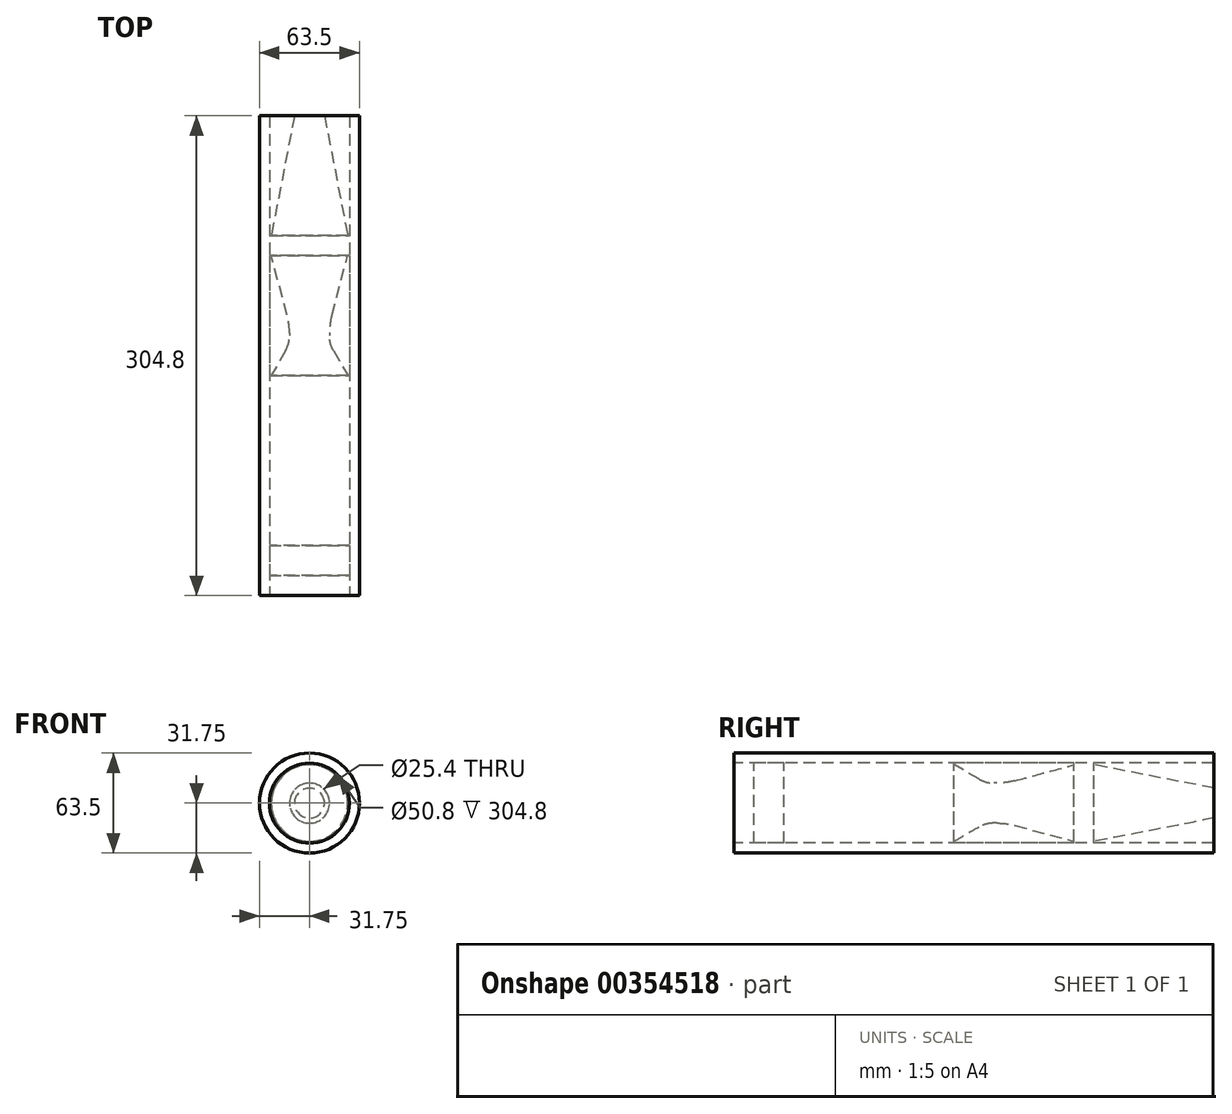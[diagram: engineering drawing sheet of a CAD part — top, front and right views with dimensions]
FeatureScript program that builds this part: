
annotation { "Feature Type Name" : "Feature", "Feature Type Description" : "" }
export const myFeature = defineFeature(function(context is Context, id is Id, definition is map)
    precondition{}
    {
        {
            var Q0;
            Q0=qCreatedBy(makeId("Front.planeOp"),FACE);
            var sketch = newSketch(context, id + "F0", { "sketchPlane" : qUnion([Q0])});
            skCircle(sketch, "E0", {"center": v(0, 0) * mm, "radius": 31.75 * mm});
            skCircle(sketch, "E1", {"center": v(0, 0) * mm, "radius": 25.4 * mm});
            skCircle(sketch, "E2", {"center": v(0, 0) * mm, "radius": 12.7 * mm});
            skCircle(sketch, "E3", {"center": v(0, 0) * mm, "radius": 9.53 * mm});
            skSolve(sketch);
        }
        {
            var Q0;
            Q0 = qSketchRegion(id + "F0", true);
            extrude(context, id + "F1", {"entities" : qUnion([Q0]), "oppositeDirection" : true, "offsetDistance" : 25.4 * mm, "depth" : 304.8 * mm});
        }
        {
            var Q0;
            Q0=makeQuery(id+"F0.imprint","IMPRINT",FACE,{"disambiguationData":[TD([[makeQuery(id+"F0.imprint","IMPRINT",EDGE,{"derivedFrom":sQuery(id+"F0.wireOp",EDGE,"E1")}),1.0]])]});
            extrude(context, id + "F2", {"entities" : qUnion([Q0]), "oppositeDirection" : true, "depth" : 76.2 * mm, "offsetDistance" : 25.4 * mm});
        }
        {
            var Q0;
            Q0=makeQuery(id+"F2.opExtrude","SWEPT_BODY",BODY,{"disambiguationData":[OSD([sQuery(id+"F0.wireOp",EDGE,"E1"),sQuery(id+"F0.wireOp",EDGE,"E2")])]});
            transform(context, id + "F3", {"entities" : qUnion([Q0]), "transformType" : TransformType.TRANSLATION_3D, "dx" : 127 * mm, "dy" : 0 * mm, "dz" : 0 * mm, "makeCopy" : false});
        }
        {
            var Q0;
            Q0=makeQuery(id+"F0.imprint","IMPRINT",FACE,{"disambiguationData":[TD([[makeQuery(id+"F0.imprint","IMPRINT",EDGE,{"derivedFrom":sQuery(id+"F0.wireOp",EDGE,"E1")}),1.0]])]});
            var Q1;
            Q1=makeQuery(id+"F0.imprint","IMPRINT",FACE,{"disambiguationData":[TD([[makeQuery(id+"F0.imprint","IMPRINT",EDGE,{"derivedFrom":sQuery(id+"F0.wireOp",EDGE,"E2")}),1.0]])]});
            extrude(context, id + "F4", {"entities" : qUnion([Q0, Q1]), "oppositeDirection" : true, "depth" : 76.2 * mm, "offsetDistance" : 25.4 * mm});
        }
        {
            var Q0;
            Q0=makeQuery(id+"F4.opExtrude","SWEPT_BODY",BODY,{"disambiguationData":[OSD([sQuery(id+"F0.wireOp",EDGE,"E1"),sQuery(id+"F0.wireOp",EDGE,"E3")])]});
            transform(context, id + "F5", {"entities" : qUnion([Q0]), "transformType" : TransformType.TRANSLATION_3D, "dx" : -127 * mm, "dy" : 0 * mm, "dz" : 0 * mm, "makeCopy" : false});
        }
        {
            var Q0;
            Q0=makeQuery(id+"F2.opExtrude","CAP_EDGE",EDGE,{"disambiguationData":[OSD([sQuery(id+"F0.wireOp",EDGE,"E2")])],"isStart":true});
            chamfer(context, id + "F6", {"entities" : qUnion([Q0]), "chamferType" : ChamferType.OFFSET_ANGLE, "width" : 20.32 * mm, "oppositeDirection" : false, "angle" : 30 * degree, "tangentPropagation" : true});
        }
        {
            var Q0;
            Q0=makeQuery(id+"F2.opExtrude","CAP_EDGE",EDGE,{"disambiguationData":[OSD([sQuery(id+"F0.wireOp",EDGE,"E2")])],"isStart":false});
            chamfer(context, id + "F7", {"entities" : qUnion([Q0]), "chamferType" : ChamferType.OFFSET_ANGLE, "width" : 43.18 * mm, "oppositeDirection" : true, "angle" : 15 * degree, "tangentPropagation" : true});
        }
        {
            var Q0;
            {var subQ0=sQuery(id+"F0.wireOp",EDGE,"E2");Q0=makeQuery(id+"F6.opChamfer","BLEND_EDGE",EDGE,{"blendedFrom":[makeQuery(id+"F2.opExtrude","CAP_EDGE",EDGE,{"disambiguationData":[OSD([subQ0])],"isStart":true}),makeQuery(id+"F2.opExtrude","SWEPT_FACE",FACE,{"disambiguationData":[OSD([subQ0])]})],"blendedInto":[makeQuery(id+"F2.opExtrude","SWEPT_FACE",FACE,{"disambiguationData":[OSD([subQ0])]})]});}
            fillet(context, id + "F8", {"entities" : qUnion([Q0]), "tangentPropagation" : true, "radius" : 19.05 * mm, "defaultsChanged" : true, "vertexSettings" : [], "allowEdgeOverflow" : false});
        }
        {
            var Q0;
            {var subQ0=sQuery(id+"F0.wireOp",EDGE,"E2");Q0=makeQuery(id+"F7.opChamfer","BLEND_EDGE",EDGE,{"blendedFrom":[makeQuery(id+"F2.opExtrude","CAP_EDGE",EDGE,{"disambiguationData":[OSD([subQ0])],"isStart":false}),makeQuery(id+"F2.opExtrude","SWEPT_FACE",FACE,{"disambiguationData":[OSD([subQ0])]})],"blendedInto":[makeQuery(id+"F2.opExtrude","SWEPT_FACE",FACE,{"disambiguationData":[OSD([subQ0])]})]});}
            fillet(context, id + "F9", {"entities" : qUnion([Q0]), "tangentPropagation" : true, "radius" : 44.45 * mm, "defaultsChanged" : true, "vertexSettings" : [], "allowEdgeOverflow" : false});
        }
        {
            var Q0;
            Q0=makeQuery(id+"F4.opExtrude","CAP_EDGE",EDGE,{"disambiguationData":[OSD([sQuery(id+"F0.wireOp",EDGE,"E3")])],"isStart":true});
            chamfer(context, id + "F10", {"entities" : qUnion([Q0]), "chamferType" : ChamferType.OFFSET_ANGLE, "width" : 76.2 * mm, "oppositeDirection" : false, "angle" : 11 * degree, "tangentPropagation" : true});
        }
        {
            var Q0;
            Q0=makeQuery(id+"F4.opExtrude","SWEPT_BODY",BODY,{"disambiguationData":[OSD([sQuery(id+"F0.wireOp",EDGE,"E1"),sQuery(id+"F0.wireOp",EDGE,"E3")])]});
            transform(context, id + "F11", {"entities" : qUnion([Q0]), "transformType" : TransformType.TRANSLATION_3D, "dx" : 127 * mm, "dy" : 228.6 * mm, "dz" : 0 * mm, "makeCopy" : false});
        }
        {
            var Q0;
            Q0=makeQuery(id+"F2.opExtrude","SWEPT_BODY",BODY,{"disambiguationData":[OSD([sQuery(id+"F0.wireOp",EDGE,"E1"),sQuery(id+"F0.wireOp",EDGE,"E2")])]});
            transform(context, id + "F12", {"entities" : qUnion([Q0]), "transformType" : TransformType.TRANSLATION_3D, "dx" : -127 * mm, "dy" : 139.7 * mm, "dz" : 0 * mm, "makeCopy" : false});
        }
        {
            var Q0;
            Q0=makeQuery(id+"F0.imprint","IMPRINT",FACE,{"disambiguationData":[TD([[makeQuery(id+"F0.imprint","IMPRINT",EDGE,{"derivedFrom":sQuery(id+"F0.wireOp",EDGE,"E1")}),1.0]])]});
            var Q1;
            Q1=makeQuery(id+"F0.imprint","IMPRINT",FACE,{"disambiguationData":[TD([[makeQuery(id+"F0.imprint","IMPRINT",EDGE,{"derivedFrom":sQuery(id+"F0.wireOp",EDGE,"E2")}),1.0]])]});
            var Q2;
            Q2=makeQuery(id+"F0.imprint","IMPRINT",FACE,{"disambiguationData":[TD([[makeQuery(id+"F0.imprint","IMPRINT",EDGE,{"derivedFrom":sQuery(id+"F0.wireOp",EDGE,"E3")}),1.0]])]});
            extrude(context, id + "F13", {"entities" : qUnion([Q0, Q1, Q2]), "oppositeDirection" : true, "depth" : 19.05 * mm, "offsetDistance" : 25.4 * mm});
        }
        {
            var Q0;
            Q0=makeQuery(id+"F13.opExtrude","SWEPT_BODY",BODY,{"disambiguationData":[OSD([sQuery(id+"F0.wireOp",EDGE,"E1")])]});
            transform(context, id + "F14", {"entities" : qUnion([Q0]), "transformType" : TransformType.TRANSLATION_3D, "dx" : 0 * mm, "dy" : 12.7 * mm, "dz" : 0 * mm, "makeCopy" : false});
        }
    });
